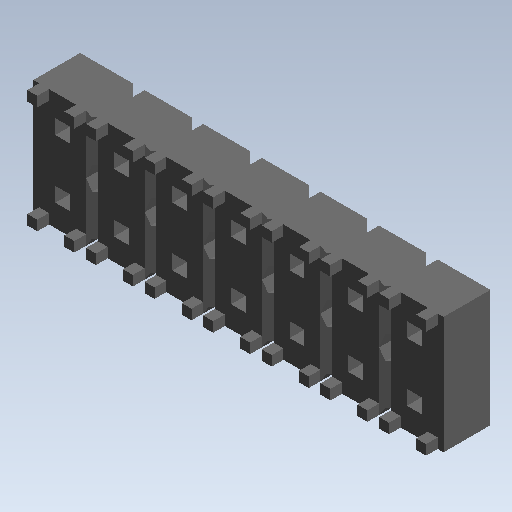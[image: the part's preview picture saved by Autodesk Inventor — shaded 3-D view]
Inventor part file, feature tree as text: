
AUTODESK INVENTOR PART (.ipt)
format: ipt  version: 2021 (Build 250183000, 183)  size: 462,848 bytes
history: native  units: mm (DEFAULTED — no unit token found)
features: extrude x9, sketch x9, other x7, pattern_linear x1
ambient origin geometry x8: Origin, YZ Plane, XZ Plane, XY Plane, X Axis, Y Axis, Z Axis, Center Point
bodies: Solid1 (feature_tree), body_XY (feature_tree), body_YZ (feature_tree), body_ZX (feature_tree), body_X (feature_tree), body_Y (feature_tree), body_Z (feature_tree), body_Center (feature_tree)
feature tree (26):
  extrude  "Extrusion1"  Depth=2.54mm TaperAngle=0.0deg
  extrude  "Extrusion2"  Depth=10.16mm TaperAngle=0.0deg
  extrude  "Extrusion3"  Depth=10.16mm TaperAngle=0.0deg
  extrude  "Extrusion4"  Depth=10.16mm TaperAngle=0.0deg
  extrude  "Extrusion5"  Depth=2.54mm TaperAngle=0.0deg
  extrude  "Extrusion6"  [1 undecoded]
  extrude  "Extrusion7"  [1 undecoded]
  extrude  "Extrusion8"  [1 undecoded]
  extrude  "Extrusion9"  [1 undecoded]
  pattern_linear  "Rectangular Pattern1"  [2 undecoded]
  other  "pin_XY"
  other  "pin_YZ"
  other  "pin_ZX"
  other  "pin_X"
  other  "pin_Y"
  other  "pin_Z"
  other  "pin_Center"
  sketch  "Sketch_1"  dims[d0=2.54mm d1=0.0mm d2=35.56mm d3=0.0mm]
  sketch  "Sketch_2"  dims[d4=35.56mm d5=0.0mm d6=10.16mm d7=0.0mm]
  sketch  "Sketch_3"  dims[d8=10.16mm d9=0.0mm d10=35.56mm d11=0.0mm]
  sketch  "Sketch_6"  dims[d12=10.16mm d13=0.0mm d14=10.16mm d15=0.0mm]
  sketch  "Sketch_9"  dims[d16=5.08mm d17=0.0mm d18=60.0mm d20=2.54mm d21=10.0mm d23=0.0mm]
  sketch  "Sketch_11"
  sketch  "Sketch_18"
  sketch  "Sketch_20"
  sketch  "Sketch_17"
note: 6 required parameter values undecoded (feature->parameter linkage not recoverable at this tier; creation-order binding heuristic only, values carry confidence <= 0.55)
